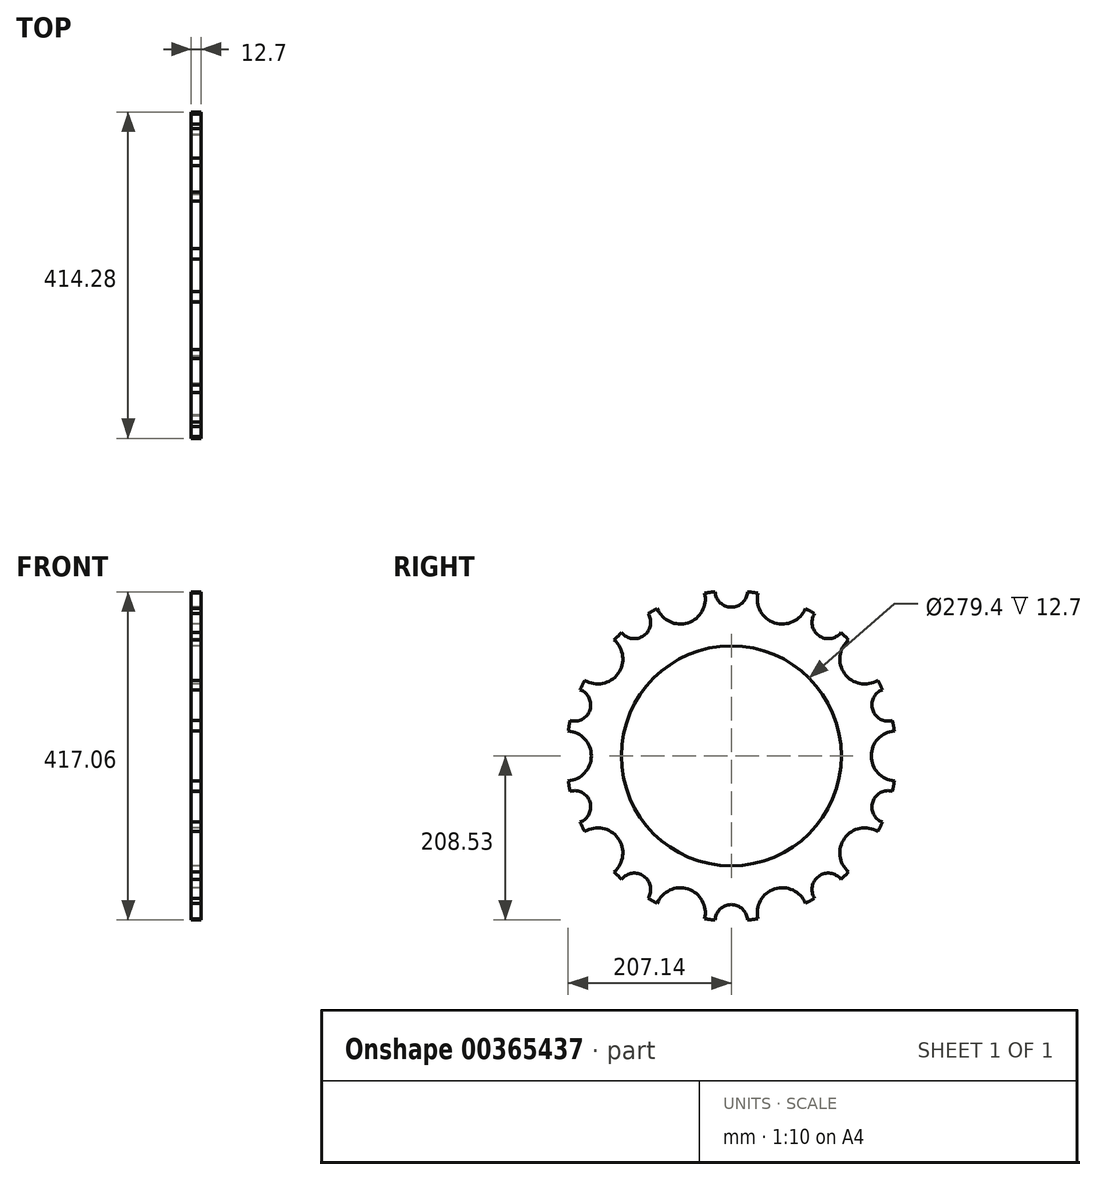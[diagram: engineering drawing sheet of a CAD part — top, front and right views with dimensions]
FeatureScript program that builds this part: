
annotation { "Feature Type Name" : "Feature", "Feature Type Description" : "" }
export const myFeature = defineFeature(function(context is Context, id is Id, definition is map)
    precondition{}
    {
        {
            var Q0;
            Q0=qCreatedBy(makeId("Right.planeOp"),FACE);
            var sketch = newSketch(context, id + "F0", { "sketchPlane" : qUnion([Q0])});
            skArc(sketch, "E0", {"start": v(-20.61, 208.53) * mm, "mid": v(-27.27, 207.77) * mm, "end": v(-33.9, 206.79) * mm});
            skCircle(sketch, "E1", {"center": v(0, 0) * mm, "radius": 139.7 * mm});
            skLineSegment(sketch, "E2", {"start": v(0, 0) * mm, "end": v(0, 209.55) * mm, "construction": true});
            skArc(sketch, "E3", {"start": v(-20.61, 208.53) * mm, "mid": v(0, 188.91) * mm, "end": v(20.61, 208.53) * mm});
            skArc(sketch, "E4.1.0", {"start": v(-139.25, 156.6) * mm, "mid": v(-111.04, 152.83) * mm, "end": v(-105.9, 180.82) * mm});
            skArc(sketch, "E4.2.0", {"start": v(-204.7, 44.84) * mm, "mid": v(-179.67, 58.38) * mm, "end": v(-191.96, 84.04) * mm});
            skArc(sketch, "E4.3.0", {"start": v(-191.96, -84.04) * mm, "mid": v(-179.67, -58.38) * mm, "end": v(-204.7, -44.84) * mm});
            skArc(sketch, "E4.4.0", {"start": v(-105.9, -180.82) * mm, "mid": v(-111.04, -152.83) * mm, "end": v(-139.25, -156.6) * mm});
            skArc(sketch, "E4.5.0", {"start": v(20.61, -208.53) * mm, "mid": v(0, -188.91) * mm, "end": v(-20.61, -208.53) * mm});
            skArc(sketch, "E4.6.0", {"start": v(139.25, -156.6) * mm, "mid": v(111.04, -152.83) * mm, "end": v(105.9, -180.82) * mm});
            skArc(sketch, "E4.7.0", {"start": v(204.7, -44.84) * mm, "mid": v(179.67, -58.38) * mm, "end": v(191.96, -84.04) * mm});
            skArc(sketch, "E4.8.0", {"start": v(191.96, 84.04) * mm, "mid": v(179.67, 58.38) * mm, "end": v(204.7, 44.84) * mm});
            skArc(sketch, "E4.9.0", {"start": v(105.9, 180.82) * mm, "mid": v(111.04, 152.83) * mm, "end": v(139.25, 156.6) * mm});
            skArc(sketch, "E5.trimOffspring", {"start": v(-139.25, 156.6) * mm, "mid": v(-144.19, 152.06) * mm, "end": v(-148.98, 147.37) * mm});
            skArc(sketch, "E6.trimOffspring", {"start": v(-204.7, 44.84) * mm, "mid": v(-206.03, 38.27) * mm, "end": v(-207.14, 31.66) * mm});
            skArc(sketch, "E7.trimOffspring", {"start": v(-191.96, -84.04) * mm, "mid": v(-189.17, -90.14) * mm, "end": v(-186.2, -96.14) * mm});
            skArc(sketch, "E8.trimOffspring", {"start": v(-105.9, -180.82) * mm, "mid": v(-100.06, -184.12) * mm, "end": v(-94.12, -187.22) * mm});
            skArc(sketch, "E9.trimOffspring", {"start": v(20.61, -208.53) * mm, "mid": v(27.27, -207.77) * mm, "end": v(33.9, -206.79) * mm});
            skArc(sketch, "E10.trimOffspring", {"start": v(139.25, -156.6) * mm, "mid": v(144.19, -152.06) * mm, "end": v(148.98, -147.37) * mm});
            skArc(sketch, "E11.trimOffspring", {"start": v(204.7, -44.84) * mm, "mid": v(206.03, -38.27) * mm, "end": v(207.14, -31.66) * mm});
            skArc(sketch, "E12.trimOffspring", {"start": v(191.96, 84.04) * mm, "mid": v(189.17, 90.14) * mm, "end": v(186.2, 96.14) * mm});
            skArc(sketch, "E13.trimOffspring", {"start": v(105.9, 180.82) * mm, "mid": v(100.06, 184.12) * mm, "end": v(94.12, 187.22) * mm});
            skArc(sketch, "E14", {"start": v(33.9, 206.79) * mm, "mid": v(54.94, 169.1) * mm, "end": v(94.12, 187.22) * mm});
            skArc(sketch, "E15.trimOffspring", {"start": v(33.9, 206.79) * mm, "mid": v(27.27, 207.77) * mm, "end": v(20.61, 208.53) * mm});
            skArc(sketch, "E16.1.0", {"start": v(-94.12, 187.22) * mm, "mid": v(-54.94, 169.1) * mm, "end": v(-33.9, 206.79) * mm});
            skArc(sketch, "E16.2.0", {"start": v(-186.2, 96.14) * mm, "mid": v(-143.84, 104.5) * mm, "end": v(-148.98, 147.37) * mm});
            skArc(sketch, "E16.3.0", {"start": v(-207.14, -31.66) * mm, "mid": v(-177.8, 0) * mm, "end": v(-207.14, 31.66) * mm});
            skArc(sketch, "E16.4.0", {"start": v(-148.98, -147.37) * mm, "mid": v(-143.84, -104.5) * mm, "end": v(-186.2, -96.14) * mm});
            skArc(sketch, "E16.5.0", {"start": v(-33.9, -206.79) * mm, "mid": v(-54.94, -169.1) * mm, "end": v(-94.12, -187.22) * mm});
            skArc(sketch, "E16.6.0", {"start": v(94.12, -187.22) * mm, "mid": v(54.94, -169.1) * mm, "end": v(33.9, -206.79) * mm});
            skArc(sketch, "E16.7.0", {"start": v(186.2, -96.14) * mm, "mid": v(143.84, -104.5) * mm, "end": v(148.98, -147.37) * mm});
            skArc(sketch, "E16.8.0", {"start": v(207.14, 31.66) * mm, "mid": v(177.8, 0) * mm, "end": v(207.14, -31.66) * mm});
            skArc(sketch, "E16.9.0", {"start": v(148.98, 147.37) * mm, "mid": v(143.84, 104.5) * mm, "end": v(186.2, 96.14) * mm});
            skArc(sketch, "E17.trimOffspring", {"start": v(148.98, 147.37) * mm, "mid": v(144.19, 152.06) * mm, "end": v(139.25, 156.6) * mm});
            skArc(sketch, "E18.trimOffspring", {"start": v(207.14, 31.66) * mm, "mid": v(206.03, 38.27) * mm, "end": v(204.7, 44.84) * mm});
            skArc(sketch, "E19.trimOffspring", {"start": v(186.2, -96.14) * mm, "mid": v(189.17, -90.14) * mm, "end": v(191.96, -84.04) * mm});
            skArc(sketch, "E20.trimOffspring", {"start": v(94.12, -187.22) * mm, "mid": v(100.06, -184.12) * mm, "end": v(105.9, -180.82) * mm});
            skArc(sketch, "E21.trimOffspring", {"start": v(-33.9, -206.79) * mm, "mid": v(-27.27, -207.77) * mm, "end": v(-20.61, -208.53) * mm});
            skArc(sketch, "E22.trimOffspring", {"start": v(-148.98, -147.37) * mm, "mid": v(-144.19, -152.06) * mm, "end": v(-139.25, -156.6) * mm});
            skArc(sketch, "E23.trimOffspring", {"start": v(-207.14, -31.66) * mm, "mid": v(-206.03, -38.27) * mm, "end": v(-204.7, -44.84) * mm});
            skArc(sketch, "E24.trimOffspring", {"start": v(-186.2, 96.14) * mm, "mid": v(-189.17, 90.14) * mm, "end": v(-191.96, 84.04) * mm});
            skArc(sketch, "E25.trimOffspring", {"start": v(-94.12, 187.22) * mm, "mid": v(-100.06, 184.12) * mm, "end": v(-105.9, 180.82) * mm});
            skLineSegment(sketch, "E26", {"start": v(0, 0) * mm, "end": v(64.75, 199.3) * mm, "construction": true});
            skSolve(sketch);
        }
        {
            var Q0;
            Q0 = qSketchRegion(id + "F0", true);
            extrude(context, id + "F1", {"entities" : qUnion([Q0]), "depth" : 12.7 * mm});
        }
    });
